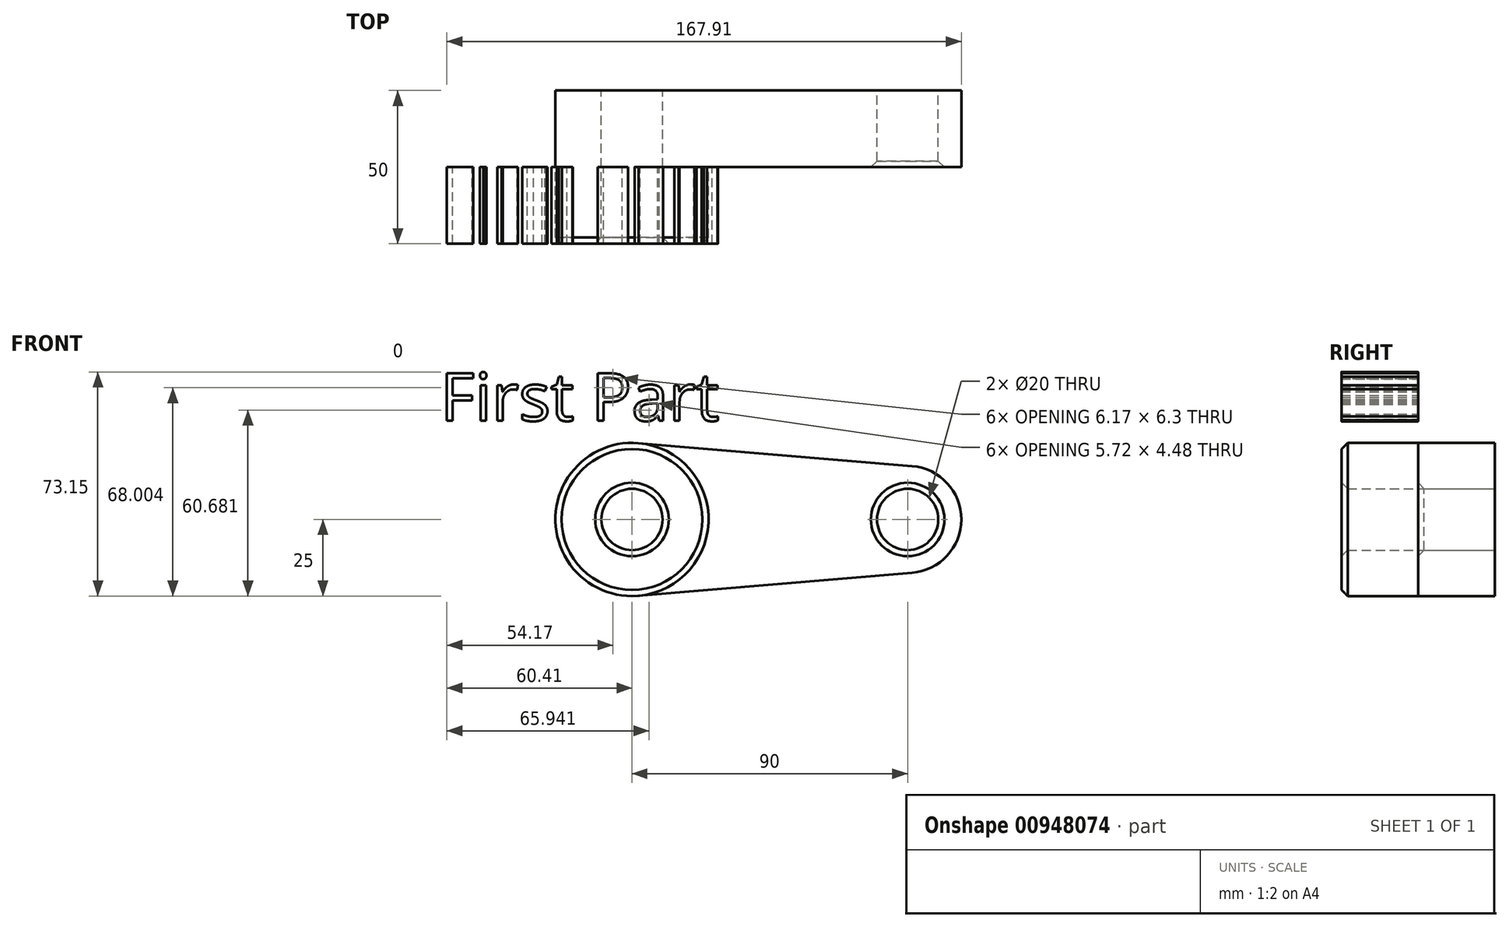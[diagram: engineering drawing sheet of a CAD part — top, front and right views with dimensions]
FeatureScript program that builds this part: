
annotation { "Feature Type Name" : "Feature", "Feature Type Description" : "" }
export const myFeature = defineFeature(function(context is Context, id is Id, definition is map)
    precondition{}
    {
        {
            var Q0;
            Q0=qCreatedBy(makeId("Front.planeOp"),FACE);
            var sketch = newSketch(context, id + "F0", { "sketchPlane" : qUnion([Q0])});
            skCircle(sketch, "E0", {"center": v(0, 0) * mm, "radius": 25 * mm});
            skCircle(sketch, "E1", {"center": v(90, 0) * mm, "radius": 17.5 * mm});
            skLineSegment(sketch, "E2", {"start": v(2.08, 24.91) * mm, "end": v(91.46, 17.44) * mm});
            skLineSegment(sketch, "E3", {"start": v(2.08, -24.91) * mm, "end": v(91.46, -17.44) * mm});
            skCircle(sketch, "E4", {"center": v(0, 0) * mm, "radius": 10 * mm});
            skCircle(sketch, "E5", {"center": v(90, 0) * mm, "radius": 10 * mm});
            skSolve(sketch);
        }
        {
            var Q0;
            Q0=qSketchRegion(id+"F0",true);
            extrude(context, id + "F1", {"entities" : qUnion([Q0]), "depth" : 25 * mm});
        }
        {
            var Q0;
            Q0=makeQuery(id+"F0.imprint","IMPRINT",FACE,{"disambiguationData":[TD([[makeQuery(id+"F0.imprint","IMPRINT",EDGE,{"derivedFrom":sQuery(id+"F0.wireOp",EDGE,"E4")}),-1.0]])]});
            extrude(context, id + "F2", {"entities" : qUnion([Q0]), "operationType" : NewBodyOperationType.ADD, "depth" : 50 * mm});
        }
        {
            var Q0;
            Q0=makeQuery(id+"F2.opExtrude","CAP_EDGE",EDGE,{"disambiguationData":[OSD([sQuery(id+"F0.wireOp",EDGE,"E0")])],"isStart":false});
            var Q1;
            Q1=makeQuery(id+"F2.opExtrude","CAP_EDGE",EDGE,{"disambiguationData":[OSD([sQuery(id+"F0.wireOp",EDGE,"E4")])],"isStart":false});
            var Q2;
            Q2=makeQuery(id+"F1.opExtrude","CAP_EDGE",EDGE,{"disambiguationData":[OSD([sQuery(id+"F0.wireOp",EDGE,"E5")])],"isStart":false});
            chamfer(context, id + "F3", {"entities" : qUnion([Q0, Q1, Q2]), "width" : 2 * mm, "tangentPropagation" : true});
        }
        {
            var Q0;
            Q0=qCreatedBy(makeId("Front.planeOp"),FACE);
            var sketch = newSketch(context, id + "F4", { "sketchPlane" : qUnion([Q0])});
            skText(sketch, "E6", { "text": "First Part\n", "fontName": "OpenSans-Regular.ttf"});
            const initialGuessF4  = {"E6": [-0.06254, 0.0322, 1, 0, 0.01565]};
            skSetInitialGuess(sketch, initialGuessF4);
            skSolve(sketch);
        }
        {
            var Q0;
            Q0 = qSketchRegion(id + "F4", true);
            extrude(context, id + "F5", {"entities" : qUnion([Q0]), "depth" : 50 * mm, "offsetDistance" : 25 * mm, "hasSecondDirection" : true, "secondDirectionOppositeDirection" : false, "secondDirectionDepth" : 25 * mm});
        }
    });
